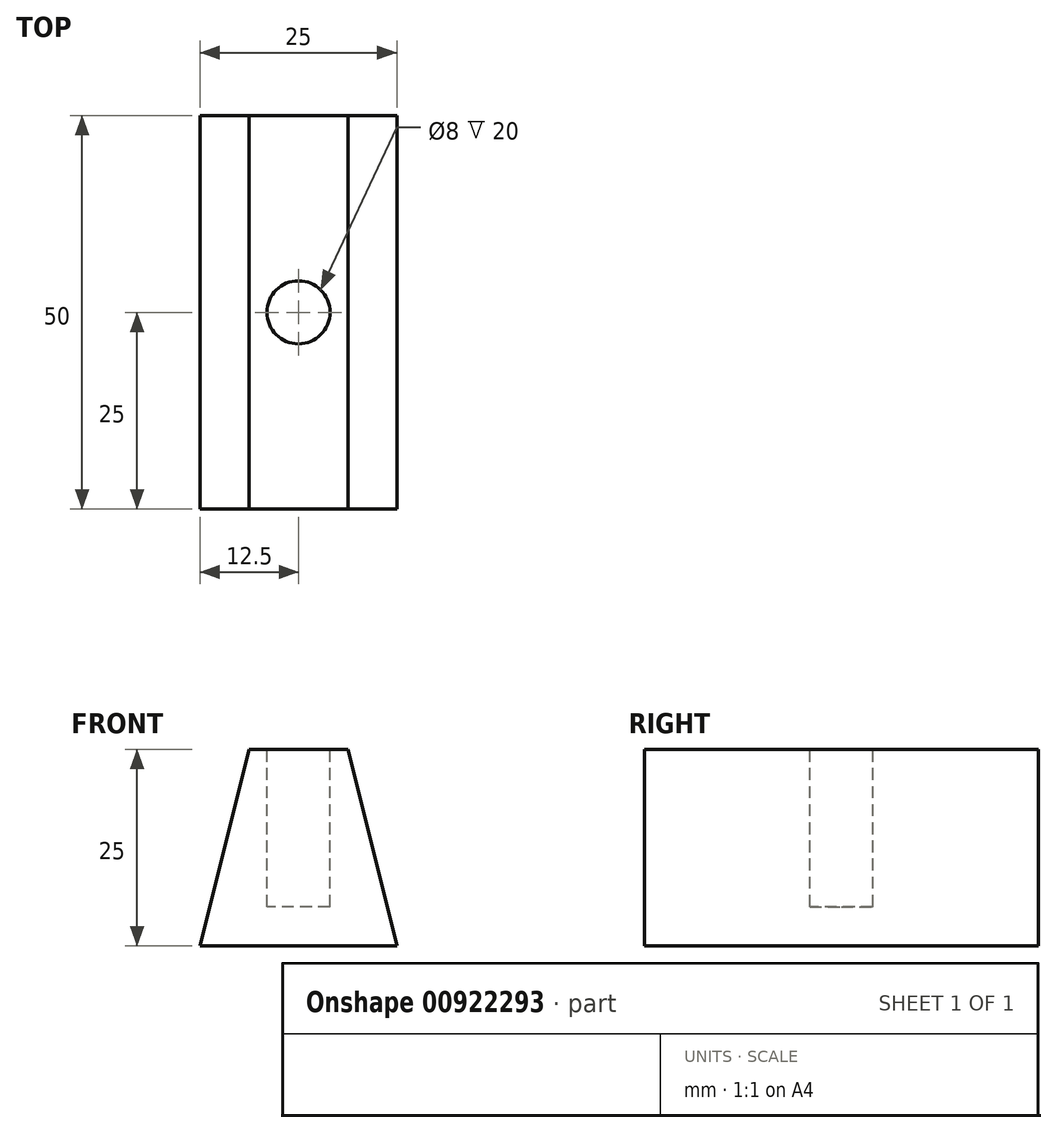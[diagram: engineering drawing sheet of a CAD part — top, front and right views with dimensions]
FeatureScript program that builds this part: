
annotation { "Feature Type Name" : "Feature", "Feature Type Description" : "" }
export const myFeature = defineFeature(function(context is Context, id is Id, definition is map)
    precondition{}
    {
        {
            var Q0;
            Q0=qCreatedBy(makeId("Front.planeOp"),FACE);
            var sketch = newSketch(context, id + "F0", { "sketchPlane" : qUnion([Q0])});
            skLineSegment(sketch, "E0", {"start": v(-12.5, 0) * mm, "end": v(12.5, 0) * mm});
            skLineSegment(sketch, "E1", {"start": v(12.5, 0) * mm, "end": v(6.27, 25) * mm});
            skLineSegment(sketch, "E2", {"start": v(6.27, 25) * mm, "end": v(-6.27, 25) * mm});
            skLineSegment(sketch, "E3", {"start": v(-6.27, 25) * mm, "end": v(-12.5, 0) * mm});
            skPoint(sketch, "E4", {"position": v(0, 0) * mm});
            skSolve(sketch);
        }
        {
            var Q0;
            Q0=makeQuery(id+"F0.imprint","IMPRINT",FACE,{"disambiguationData":[TD([[makeQuery(id+"F0.imprint","IMPRINT",EDGE,{"derivedFrom":sQuery(id+"F0.wireOp",EDGE,"E0")}),1.0]])]});
            extrude(context, id + "F1", {"entities" : qUnion([Q0]), "oppositeDirection" : true, "depth" : 50 * mm, "offsetDistance" : 25 * mm});
        }
        {
            var Q0;
            Q0=makeQuery(id+"F1.opExtrude","SWEPT_FACE",FACE,{"disambiguationData":[OSD([sQuery(id+"F0.wireOp",EDGE,"E2")])]});
            var sketch = newSketch(context, id + "F2", { "sketchPlane" : qUnion([Q0])});
            skCircle(sketch, "E5", {"center": v(0, 25) * mm, "radius": 4 * mm});
            skPoint(sketch, "E5.centerSnap0", {"position": v(-6.27, 25) * mm});
            skSolve(sketch);
        }
        {
            var Q0;
            Q0=makeQuery(id+"F2.imprint","IMPRINT",FACE,{"disambiguationData":[TD([[makeQuery(id+"F2.imprint","IMPRINT",EDGE,{"derivedFrom":sQuery(id+"F2.wireOp",EDGE,"E5")}),1.0]])]});
            extrude(context, id + "F3", {"entities" : qUnion([Q0]), "operationType" : NewBodyOperationType.REMOVE, "oppositeDirection" : true, "depth" : 20 * mm, "offsetDistance" : 25 * mm});
        }
    });
